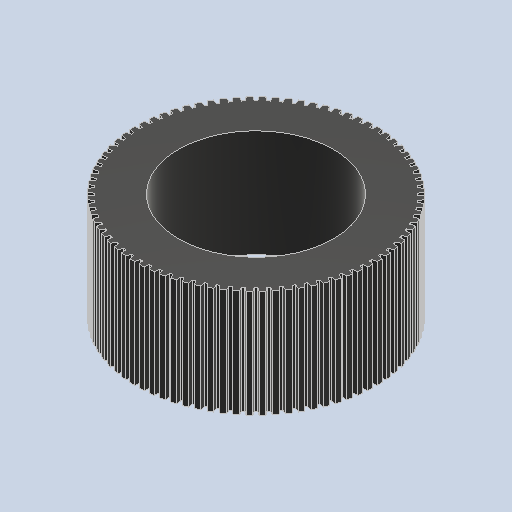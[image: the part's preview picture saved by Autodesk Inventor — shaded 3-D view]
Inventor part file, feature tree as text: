
AUTODESK INVENTOR PART (.ipt)
format: ipt  version: 2023 (Build 270158030, 158C)  size: 581,120 bytes
history: native  units: mm
features: extrude x3, sketch x3, other x1
ambient origin geometry x8: Origin, YZ Plane, XZ Plane, XY Plane, X Axis, Y Axis, Z Axis, Center Point
bodies: Body1 (feature_tree)
feature tree (7):
  other  "ソリッド1"
  extrude  "押し出し1"  Depth=10.0mm
  extrude  "押し出し2"  Depth=4.5mm TaperAngle=0.0deg
  extrude  "押し出し3"  Depth=6.5mm
  sketch  "スケッチ1"
  sketch  "スケッチ2"
  sketch  "スケッチ3"
